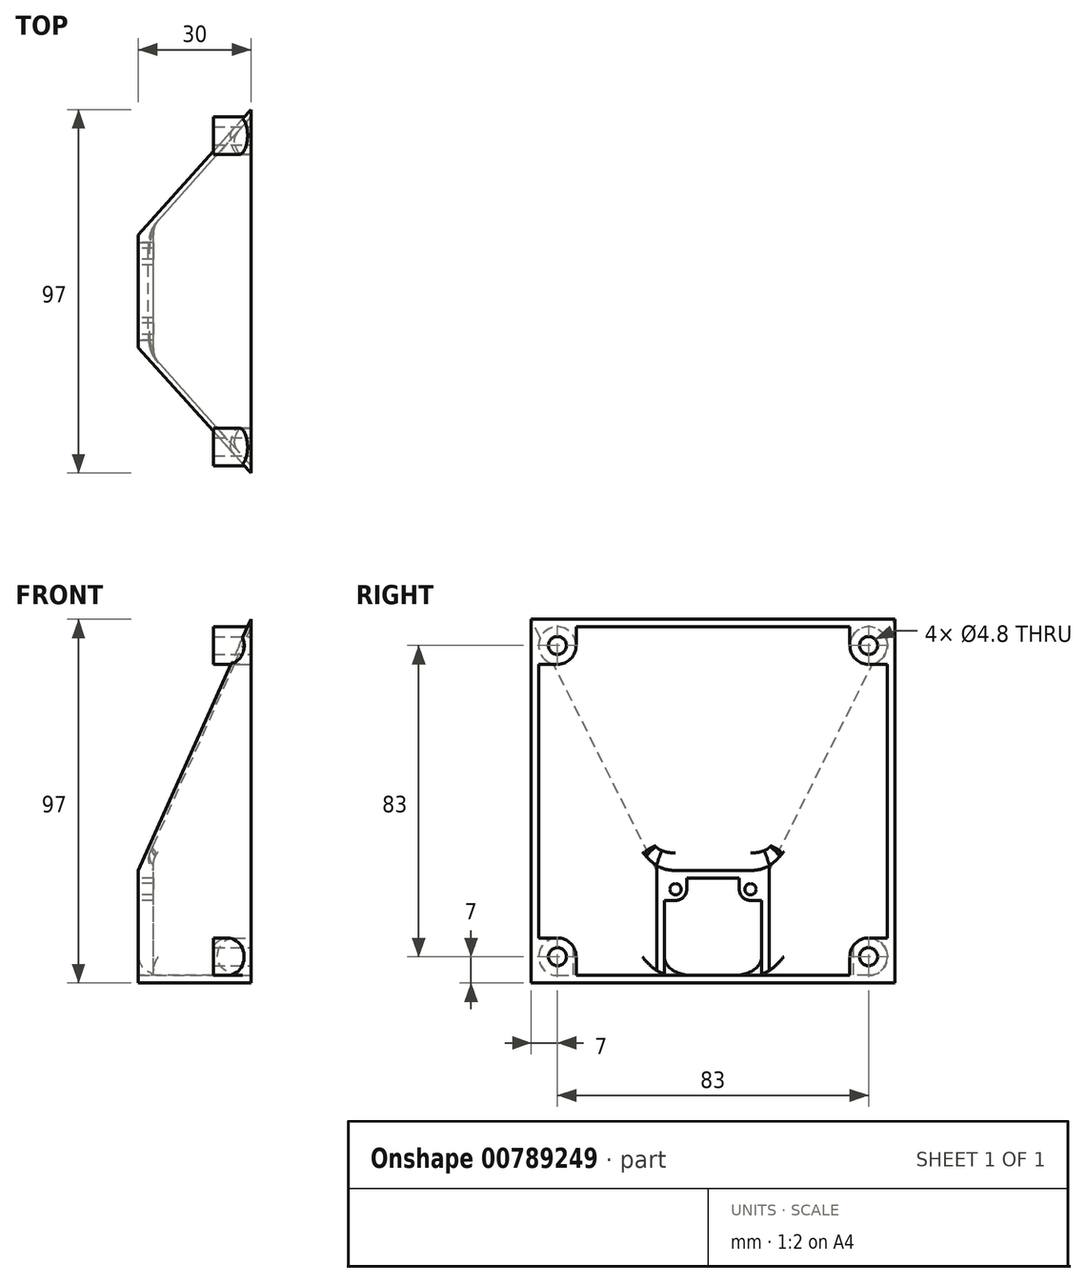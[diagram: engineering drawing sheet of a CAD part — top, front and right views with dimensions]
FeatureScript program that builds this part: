
annotation { "Feature Type Name" : "Feature", "Feature Type Description" : "" }
export const myFeature = defineFeature(function(context is Context, id is Id, definition is map)
    precondition{}
    {
        {
            var Q0;
            Q0=qCreatedBy(makeId("Right.planeOp"),FACE);
            var sketch = newSketch(context, id + "F0", { "sketchPlane" : qUnion([Q0])});
            skLineSegment(sketch, "E0.bottom", {"start": v(-15, 0) * mm, "end": v(15, 0) * mm});
            skLineSegment(sketch, "E0.top", {"start": v(-15, 30) * mm, "end": v(15, 30) * mm});
            skLineSegment(sketch, "E0.left", {"start": v(-15, 0) * mm, "end": v(-15, 30) * mm});
            skLineSegment(sketch, "E0.right", {"start": v(15, 0) * mm, "end": v(15, 30) * mm});
            skLineSegment(sketch, "E1.0", {"start": v(-13, 2) * mm, "end": v(-13, 28) * mm});
            skLineSegment(sketch, "E1.1", {"start": v(-13, 2) * mm, "end": v(13, 2) * mm});
            skLineSegment(sketch, "E1.2", {"start": v(13, 2) * mm, "end": v(13, 28) * mm});
            skLineSegment(sketch, "E1.3", {"start": v(-13, 28) * mm, "end": v(13, 28) * mm});
            skLineSegment(sketch, "E2.bottom", {"start": v(-13, 28) * mm, "end": v(-7, 28) * mm});
            skLineSegment(sketch, "E2.top", {"start": v(-13, 22) * mm, "end": v(-7, 22) * mm});
            skLineSegment(sketch, "E2.left", {"start": v(-13, 28) * mm, "end": v(-13, 22) * mm});
            skLineSegment(sketch, "E2.right", {"start": v(-7, 28) * mm, "end": v(-7, 22) * mm});
            skLineSegment(sketch, "E3.bottom", {"start": v(13, 28) * mm, "end": v(7, 28) * mm});
            skLineSegment(sketch, "E3.top", {"start": v(13, 22) * mm, "end": v(7, 22) * mm});
            skLineSegment(sketch, "E3.left", {"start": v(13, 28) * mm, "end": v(13, 22) * mm});
            skLineSegment(sketch, "E3.right", {"start": v(7, 28) * mm, "end": v(7, 22) * mm});
            skCircle(sketch, "E4", {"center": v(-10, 25) * mm, "radius": 3 * mm});
            skPoint(sketch, "E4.centerSnap0", {"position": v(-7, 25) * mm});
            skCircle(sketch, "E5", {"center": v(10, 25) * mm, "radius": 3 * mm});
            skPoint(sketch, "E5.centerSnap0", {"position": v(7, 25) * mm});
            skCircle(sketch, "E6", {"center": v(10, 25) * mm, "radius": 1.5 * mm});
            skCircle(sketch, "E7", {"center": v(-10, 25) * mm, "radius": 1.5 * mm});
            skSolve(sketch);
        }
        {
            var Q0;
            Q0=qCreatedBy(makeId("Right.planeOp"),FACE);
            cPlane(context, id + "F1", {"entities" : qUnion([Q0]), "cplaneType" : CPlaneType.OFFSET, "offset" : 30 * mm, "width" : 150 * mm, "height" : 150 * mm});
        }
        {
            var Q0;
            Q0=qCreatedBy(id+"F1.planeOp",FACE);
            var sketch = newSketch(context, id + "F2", { "sketchPlane" : qUnion([Q0])});
            skLineSegment(sketch, "E8.bottom", {"start": v(-48.5, 0) * mm, "end": v(48.5, 0) * mm});
            skLineSegment(sketch, "E8.top", {"start": v(-48.5, 97) * mm, "end": v(48.5, 97) * mm});
            skLineSegment(sketch, "E8.left", {"start": v(-48.5, 0) * mm, "end": v(-48.5, 97) * mm});
            skLineSegment(sketch, "E8.right", {"start": v(48.5, 0) * mm, "end": v(48.5, 97) * mm});
            skLineSegment(sketch, "E9.0", {"start": v(-46.5, 2) * mm, "end": v(-46.5, 95) * mm});
            skLineSegment(sketch, "E9.1", {"start": v(-46.5, 2) * mm, "end": v(46.5, 2) * mm});
            skLineSegment(sketch, "E9.2", {"start": v(46.5, 2) * mm, "end": v(46.5, 95) * mm});
            skLineSegment(sketch, "E9.3", {"start": v(-46.5, 95) * mm, "end": v(46.5, 95) * mm});
            skLineSegment(sketch, "E10.bottom", {"start": v(-46.5, 95) * mm, "end": v(-36.5, 95) * mm});
            skLineSegment(sketch, "E10.top", {"start": v(-46.5, 85) * mm, "end": v(-36.5, 85) * mm});
            skLineSegment(sketch, "E10.left", {"start": v(-46.5, 95) * mm, "end": v(-46.5, 85) * mm});
            skLineSegment(sketch, "E10.right", {"start": v(-36.5, 95) * mm, "end": v(-36.5, 85) * mm});
            skLineSegment(sketch, "E11.bottom", {"start": v(46.5, 95) * mm, "end": v(36.5, 95) * mm});
            skLineSegment(sketch, "E11.top", {"start": v(46.5, 85) * mm, "end": v(36.5, 85) * mm});
            skLineSegment(sketch, "E11.left", {"start": v(46.5, 95) * mm, "end": v(46.5, 85) * mm});
            skLineSegment(sketch, "E11.right", {"start": v(36.5, 95) * mm, "end": v(36.5, 85) * mm});
            skLineSegment(sketch, "E12.bottom", {"start": v(46.5, 2) * mm, "end": v(36.5, 2) * mm});
            skLineSegment(sketch, "E12.top", {"start": v(46.5, 12) * mm, "end": v(36.5, 12) * mm});
            skLineSegment(sketch, "E12.left", {"start": v(46.5, 2) * mm, "end": v(46.5, 12) * mm});
            skLineSegment(sketch, "E12.right", {"start": v(36.5, 2) * mm, "end": v(36.5, 12) * mm});
            skLineSegment(sketch, "E13.bottom", {"start": v(-46.5, 2) * mm, "end": v(-36.5, 2) * mm});
            skLineSegment(sketch, "E13.top", {"start": v(-46.5, 12) * mm, "end": v(-36.5, 12) * mm});
            skLineSegment(sketch, "E13.left", {"start": v(-46.5, 2) * mm, "end": v(-46.5, 12) * mm});
            skLineSegment(sketch, "E13.right", {"start": v(-36.5, 2) * mm, "end": v(-36.5, 12) * mm});
            skCircle(sketch, "E14", {"center": v(-41.5, 90) * mm, "radius": 5 * mm});
            skPoint(sketch, "E14.centerSnap0", {"position": v(-46.5, 90) * mm});
            skCircle(sketch, "E15", {"center": v(41.5, 90) * mm, "radius": 5 * mm});
            skPoint(sketch, "E15.centerSnap0", {"position": v(41.5, 85) * mm});
            skCircle(sketch, "E16", {"center": v(-41.5, 7) * mm, "radius": 5 * mm});
            skCircle(sketch, "E17", {"center": v(41.5, 7) * mm, "radius": 5 * mm});
            skPoint(sketch, "E17.centerSnap0", {"position": v(41.5, 2) * mm});
            skCircle(sketch, "E18", {"center": v(-41.5, 90) * mm, "radius": 2.4 * mm});
            skCircle(sketch, "E19", {"center": v(41.5, 90) * mm, "radius": 2.4 * mm});
            skCircle(sketch, "E20", {"center": v(41.5, 7) * mm, "radius": 2.4 * mm});
            skCircle(sketch, "E21", {"center": v(-41.5, 7) * mm, "radius": 2.4 * mm});
            skSolve(sketch);
        }
        {
            var Q0;
            Q0=qCreatedBy(makeId("Right.planeOp"),FACE);
            var sketch = newSketch(context, id + "F3", { "sketchPlane" : qUnion([Q0])});
            skLineSegment(sketch, "E22.bottom", {"start": v(-15, 0) * mm, "end": v(15, 0) * mm});
            skLineSegment(sketch, "E22.top", {"start": v(-15, 30) * mm, "end": v(15, 30) * mm});
            skLineSegment(sketch, "E22.left", {"start": v(-15, 0) * mm, "end": v(-15, 30) * mm});
            skLineSegment(sketch, "E22.right", {"start": v(15, 0) * mm, "end": v(15, 30) * mm});
            skSolve(sketch);
        }
        {
            var Q0;
            Q0=qCreatedBy(id+"F1.planeOp",FACE);
            var sketch = newSketch(context, id + "F4", { "sketchPlane" : qUnion([Q0])});
            skLineSegment(sketch, "E23.bottom", {"start": v(-48.5, 0) * mm, "end": v(48.5, 0) * mm});
            skLineSegment(sketch, "E23.top", {"start": v(-48.5, 97) * mm, "end": v(48.5, 97) * mm});
            skLineSegment(sketch, "E23.left", {"start": v(-48.5, 0) * mm, "end": v(-48.5, 97) * mm});
            skLineSegment(sketch, "E23.right", {"start": v(48.5, 0) * mm, "end": v(48.5, 97) * mm});
            skSolve(sketch);
        }
        {
            var Q0;
            Q0=qCreatedBy(makeId("Right.planeOp"),FACE);
            var sketch = newSketch(context, id + "F5", { "sketchPlane" : qUnion([Q0])});
            skLineSegment(sketch, "E24.bottom", {"start": v(-13, 2) * mm, "end": v(13, 2) * mm});
            skLineSegment(sketch, "E24.top", {"start": v(-13, 28) * mm, "end": v(13, 28) * mm});
            skLineSegment(sketch, "E24.left", {"start": v(-13, 2) * mm, "end": v(-13, 28) * mm});
            skLineSegment(sketch, "E24.right", {"start": v(13, 2) * mm, "end": v(13, 28) * mm});
            skSolve(sketch);
        }
        {
            var Q0;
            Q0=qCreatedBy(id+"F1.planeOp",FACE);
            var sketch = newSketch(context, id + "F6", { "sketchPlane" : qUnion([Q0])});
            skLineSegment(sketch, "E25.bottom", {"start": v(-46.5, 2) * mm, "end": v(46.5, 2) * mm});
            skLineSegment(sketch, "E25.top", {"start": v(-46.5, 95) * mm, "end": v(46.5, 95) * mm});
            skLineSegment(sketch, "E25.left", {"start": v(-46.5, 2) * mm, "end": v(-46.5, 95) * mm});
            skLineSegment(sketch, "E25.right", {"start": v(46.5, 2) * mm, "end": v(46.5, 95) * mm});
            skSolve(sketch);
        }
        {
            var Q0;
            Q0 = qSketchRegion(id + "F3", true);
            var Q1;
            Q1 = qSketchRegion(id + "F4", true);
            loft(context, id + "F7", {"sheetProfilesArray" : [{ "sheetProfileEntities" : qUnion([Q0]) }, { "sheetProfileEntities" : qUnion([Q1]) }]});
        }
        {
            var Q1;
            Q1 = qSketchRegion(id + "F5", true);
            var Q2;
            Q2 = qSketchRegion(id + "F6", true);
            loft(context, id + "F8", {"operationType" : NewBodyOperationType.REMOVE, "sheetProfilesArray" : [{ "sheetProfileEntities" : qUnion([Q1]) }, { "sheetProfileEntities" : qUnion([Q2]) }]});
        }
        {
            var Q0;
            Q0=makeQuery(id+"F2.imprint","IMPRINT",FACE,{"disambiguationData":[TD([[makeQuery(id+"F2.imprint","IMPRINT",EDGE,{"derivedFrom":sQuery(id+"F2.wireOp",EDGE,"E18")}),-1.0]])]});
            var Q1;
            {var subQ0=sQuery(id+"F2.wireOp",EDGE,"E10.right");var subQ1=sQuery(id+"F2.wireOp",EDGE,"E9.3");var subQ2=makeQuery(id+"F2.imprint","INTERSECT",VERTEX,{"derivedFrom":[subQ1,subQ0]});Q1=makeQuery(id+"F2.imprint","IMPRINT",FACE,{"disambiguationData":[TD([[makeQuery(id+"F2.imprint","IMPRINT",EDGE,{"disambiguationData":[TD([[subQ2,1.0]])],"derivedFrom":subQ1}),-1.0]])]});}
            var Q2;
            {var subQ0=sQuery(id+"F2.wireOp",EDGE,"E9.3");var subQ1=sQuery(id+"F2.wireOp",EDGE,"E9.0");var subQ2=makeQuery(id+"F2.imprint","INTERSECT",VERTEX,{"derivedFrom":[subQ1,subQ0]});Q2=makeQuery(id+"F2.imprint","IMPRINT",FACE,{"disambiguationData":[TD([[makeQuery(id+"F2.imprint","IMPRINT",EDGE,{"disambiguationData":[TD([[subQ2,1.0]])],"derivedFrom":subQ1}),-1.0]])]});}
            var Q3;
            {var subQ0=sQuery(id+"F2.wireOp",EDGE,"E10.top");var subQ1=sQuery(id+"F2.wireOp",EDGE,"E9.0");var subQ2=makeQuery(id+"F2.imprint","INTERSECT",VERTEX,{"derivedFrom":[subQ1,subQ0]});Q3=makeQuery(id+"F2.imprint","IMPRINT",FACE,{"disambiguationData":[TD([[makeQuery(id+"F2.imprint","IMPRINT",EDGE,{"disambiguationData":[TD([[subQ2,-1.0]])],"derivedFrom":subQ1}),-1.0]])]});}
            var Q4;
            Q4=makeQuery(id+"F2.imprint","IMPRINT",FACE,{"disambiguationData":[TD([[makeQuery(id+"F2.imprint","IMPRINT",EDGE,{"derivedFrom":sQuery(id+"F2.wireOp",EDGE,"E21")}),-1.0]])]});
            var Q5;
            {var subQ0=sQuery(id+"F2.wireOp",EDGE,"E13.top");var subQ1=sQuery(id+"F2.wireOp",EDGE,"E9.0");var subQ2=makeQuery(id+"F2.imprint","INTERSECT",VERTEX,{"derivedFrom":[subQ1,subQ0]});Q5=makeQuery(id+"F2.imprint","IMPRINT",FACE,{"disambiguationData":[TD([[makeQuery(id+"F2.imprint","IMPRINT",EDGE,{"disambiguationData":[TD([[subQ2,1.0]])],"derivedFrom":subQ1}),-1.0]])]});}
            var Q6;
            {var subQ0=sQuery(id+"F2.wireOp",EDGE,"E16");var subQ1=sQuery(id+"F2.wireOp",EDGE,"E9.0");var subQ2=makeQuery(id+"F2.imprint","INTERSECT",VERTEX,{"derivedFrom":[subQ1,subQ0]});Q6=makeQuery(id+"F2.imprint","IMPRINT",FACE,{"disambiguationData":[TD([[makeQuery(id+"F2.imprint","IMPRINT",EDGE,{"disambiguationData":[TD([[subQ2,1.0]])],"derivedFrom":subQ1}),-1.0]])]});}
            var Q7;
            {var subQ0=sQuery(id+"F2.wireOp",EDGE,"E13.right");var subQ1=sQuery(id+"F2.wireOp",EDGE,"E9.1");var subQ2=makeQuery(id+"F2.imprint","INTERSECT",VERTEX,{"derivedFrom":[subQ1,subQ0]});Q7=makeQuery(id+"F2.imprint","IMPRINT",FACE,{"disambiguationData":[TD([[makeQuery(id+"F2.imprint","IMPRINT",EDGE,{"disambiguationData":[TD([[subQ2,1.0]])],"derivedFrom":subQ1}),1.0]])]});}
            var Q8;
            Q8=makeQuery(id+"F2.imprint","IMPRINT",FACE,{"disambiguationData":[TD([[makeQuery(id+"F2.imprint","IMPRINT",EDGE,{"derivedFrom":sQuery(id+"F2.wireOp",EDGE,"E20")}),-1.0]])]});
            var Q9;
            {var subQ0=sQuery(id+"F2.wireOp",EDGE,"E12.right");var subQ1=sQuery(id+"F2.wireOp",EDGE,"E9.1");var subQ2=makeQuery(id+"F2.imprint","INTERSECT",VERTEX,{"derivedFrom":[subQ1,subQ0]});Q9=makeQuery(id+"F2.imprint","IMPRINT",FACE,{"disambiguationData":[TD([[makeQuery(id+"F2.imprint","IMPRINT",EDGE,{"disambiguationData":[TD([[subQ2,-1.0]])],"derivedFrom":subQ1}),1.0]])]});}
            var Q10;
            {var subQ0=sQuery(id+"F2.wireOp",EDGE,"E9.2");var subQ1=sQuery(id+"F2.wireOp",EDGE,"E9.1");var subQ2=makeQuery(id+"F2.imprint","INTERSECT",VERTEX,{"derivedFrom":[subQ1,subQ0]});Q10=makeQuery(id+"F2.imprint","IMPRINT",FACE,{"disambiguationData":[TD([[makeQuery(id+"F2.imprint","IMPRINT",EDGE,{"disambiguationData":[TD([[subQ2,1.0]])],"derivedFrom":subQ1}),1.0]])]});}
            var Q11;
            {var subQ0=sQuery(id+"F2.wireOp",EDGE,"E12.top");var subQ1=sQuery(id+"F2.wireOp",EDGE,"E9.2");var subQ2=makeQuery(id+"F2.imprint","INTERSECT",VERTEX,{"derivedFrom":[subQ1,subQ0]});Q11=makeQuery(id+"F2.imprint","IMPRINT",FACE,{"disambiguationData":[TD([[makeQuery(id+"F2.imprint","IMPRINT",EDGE,{"disambiguationData":[TD([[subQ2,1.0]])],"derivedFrom":subQ1}),1.0]])]});}
            var Q12;
            Q12=makeQuery(id+"F2.imprint","IMPRINT",FACE,{"disambiguationData":[TD([[makeQuery(id+"F2.imprint","IMPRINT",EDGE,{"derivedFrom":sQuery(id+"F2.wireOp",EDGE,"E19")}),-1.0]])]});
            var Q13;
            {var subQ0=sQuery(id+"F2.wireOp",EDGE,"E11.right");var subQ1=sQuery(id+"F2.wireOp",EDGE,"E9.3");var subQ2=makeQuery(id+"F2.imprint","INTERSECT",VERTEX,{"derivedFrom":[subQ1,subQ0]});Q13=makeQuery(id+"F2.imprint","IMPRINT",FACE,{"disambiguationData":[TD([[makeQuery(id+"F2.imprint","IMPRINT",EDGE,{"disambiguationData":[TD([[subQ2,-1.0]])],"derivedFrom":subQ1}),-1.0]])]});}
            var Q14;
            {var subQ0=sQuery(id+"F2.wireOp",EDGE,"E9.3");var subQ1=sQuery(id+"F2.wireOp",EDGE,"E9.2");var subQ2=makeQuery(id+"F2.imprint","INTERSECT",VERTEX,{"derivedFrom":[subQ1,subQ0]});Q14=makeQuery(id+"F2.imprint","IMPRINT",FACE,{"disambiguationData":[TD([[makeQuery(id+"F2.imprint","IMPRINT",EDGE,{"disambiguationData":[TD([[subQ2,1.0]])],"derivedFrom":subQ1}),1.0]])]});}
            var Q15;
            {var subQ0=sQuery(id+"F2.wireOp",EDGE,"E11.top");var subQ1=sQuery(id+"F2.wireOp",EDGE,"E9.2");var subQ2=makeQuery(id+"F2.imprint","INTERSECT",VERTEX,{"derivedFrom":[subQ1,subQ0]});Q15=makeQuery(id+"F2.imprint","IMPRINT",FACE,{"disambiguationData":[TD([[makeQuery(id+"F2.imprint","IMPRINT",EDGE,{"disambiguationData":[TD([[subQ2,-1.0]])],"derivedFrom":subQ1}),1.0]])]});}
            extrude(context, id + "F9", {"entities" : qUnion([Q0, Q1, Q2, Q3, Q4, Q5, Q6, Q7, Q8, Q9, Q10, Q11, Q12, Q13, Q14, Q15]), "operationType" : NewBodyOperationType.ADD, "oppositeDirection" : true, "depth" : 10 * mm, "offsetDistance" : 25 * mm});
        }
        {
            var Q0;
            Q0=makeQuery(id+"F0.imprint","IMPRINT",FACE,{"disambiguationData":[TD([[makeQuery(id+"F0.imprint","IMPRINT",EDGE,{"derivedFrom":sQuery(id+"F0.wireOp",EDGE,"E7")}),-1.0]])]});
            var Q1;
            {var subQ0=sQuery(id+"F0.wireOp",EDGE,"E2.right");var subQ1=sQuery(id+"F0.wireOp",EDGE,"E1.3");var subQ2=makeQuery(id+"F0.imprint","INTERSECT",VERTEX,{"derivedFrom":[subQ1,subQ0]});Q1=makeQuery(id+"F0.imprint","IMPRINT",FACE,{"disambiguationData":[TD([[makeQuery(id+"F0.imprint","IMPRINT",EDGE,{"disambiguationData":[TD([[subQ2,1.0]])],"derivedFrom":subQ1}),-1.0]])]});}
            var Q2;
            {var subQ0=sQuery(id+"F0.wireOp",EDGE,"E4");var subQ1=sQuery(id+"F0.wireOp",EDGE,"E1.0");var subQ2=makeQuery(id+"F0.imprint","INTERSECT",VERTEX,{"derivedFrom":[subQ1,subQ0]});Q2=makeQuery(id+"F0.imprint","IMPRINT",FACE,{"disambiguationData":[TD([[makeQuery(id+"F0.imprint","IMPRINT",EDGE,{"disambiguationData":[TD([[subQ2,-1.0]])],"derivedFrom":subQ1}),-1.0]])]});}
            var Q3;
            {var subQ0=sQuery(id+"F0.wireOp",EDGE,"E4");var subQ1=sQuery(id+"F0.wireOp",EDGE,"E1.0");var subQ2=makeQuery(id+"F0.imprint","INTERSECT",VERTEX,{"derivedFrom":[subQ1,subQ0]});Q3=makeQuery(id+"F0.imprint","IMPRINT",FACE,{"disambiguationData":[TD([[makeQuery(id+"F0.imprint","IMPRINT",EDGE,{"disambiguationData":[TD([[subQ2,1.0]])],"derivedFrom":subQ1}),-1.0]])]});}
            var Q4;
            {var subQ0=sQuery(id+"F0.wireOp",EDGE,"E5");var subQ1=sQuery(id+"F0.wireOp",EDGE,"E1.3");var subQ2=makeQuery(id+"F0.imprint","INTERSECT",VERTEX,{"derivedFrom":[subQ1,subQ0]});Q4=makeQuery(id+"F0.imprint","IMPRINT",FACE,{"disambiguationData":[TD([[makeQuery(id+"F0.imprint","IMPRINT",EDGE,{"disambiguationData":[TD([[subQ2,1.0]])],"derivedFrom":subQ1}),-1.0]])]});}
            var Q5;
            {var subQ0=sQuery(id+"F0.wireOp",EDGE,"E5");var subQ1=sQuery(id+"F0.wireOp",EDGE,"E1.2");var subQ2=makeQuery(id+"F0.imprint","INTERSECT",VERTEX,{"derivedFrom":[subQ1,subQ0]});Q5=makeQuery(id+"F0.imprint","IMPRINT",FACE,{"disambiguationData":[TD([[makeQuery(id+"F0.imprint","IMPRINT",EDGE,{"disambiguationData":[TD([[subQ2,-1.0]])],"derivedFrom":subQ1}),1.0]])]});}
            var Q6;
            {var subQ0=sQuery(id+"F0.wireOp",EDGE,"E5");var subQ1=sQuery(id+"F0.wireOp",EDGE,"E1.2");var subQ2=makeQuery(id+"F0.imprint","INTERSECT",VERTEX,{"derivedFrom":[subQ1,subQ0]});Q6=makeQuery(id+"F0.imprint","IMPRINT",FACE,{"disambiguationData":[TD([[makeQuery(id+"F0.imprint","IMPRINT",EDGE,{"disambiguationData":[TD([[subQ2,1.0]])],"derivedFrom":subQ1}),1.0]])]});}
            var Q7;
            Q7=makeQuery(id+"F0.imprint","IMPRINT",FACE,{"disambiguationData":[TD([[makeQuery(id+"F0.imprint","IMPRINT",EDGE,{"derivedFrom":sQuery(id+"F0.wireOp",EDGE,"E6")}),-1.0]])]});
            var Q8;
            Q8=makeQuery(id+"F0.imprint","IMPRINT",FACE,{"disambiguationData":[TD([[makeQuery(id+"F0.imprint","IMPRINT",EDGE,{"derivedFrom":sQuery(id+"F0.wireOp",EDGE,"E0.bottom")}),1.0]])]});
            extrude(context, id + "F10", {"entities" : qUnion([Q0, Q1, Q2, Q3, Q4, Q5, Q6, Q7, Q8]), "operationType" : NewBodyOperationType.ADD, "depth" : 4 * mm, "offsetDistance" : 25 * mm});
        }
        {
            var Q0;
            {var subQ6=sQuery(id+"F2.wireOp",EDGE,"E11.top");var subQ9=sQuery(id+"F6.wireOp",EDGE,"E25.right");var subQ11=sQuery(id+"F6.wireOp",EDGE,"E25.top");var subQ12=sQuery(id+"F5.wireOp",EDGE,"E24.right");var subQ14=sQuery(id+"F5.wireOp",EDGE,"E24.top");var subQ15=sQuery(id+"F6.wireOp",EDGE,"E25.bottom");var subQ16=sQuery(id+"F5.wireOp",EDGE,"E24.bottom");Q0=makeQuery(id+"F10.boolean.opBoolean","INTERSECT",EDGE,{"derivedFrom":[makeQuery(id+"F9.boolean.opBoolean","SPLIT",FACE,{"disambiguationData":[TD([makeQuery(id+"F9.opExtrude","SWEPT_FACE",FACE,{"disambiguationData":[OSD([subQ6])]})])],"derivedFrom":makeQuery(id+"F8.boolean.opBoolean","COPY",FACE,{"derivedFrom":makeQuery(id+"F8.opLoft","SWEPT_FACE",FACE,{"disambiguationData":[OSD([subQ16,subQ14,subQ12,subQ15,subQ11,subQ9])]})})}),makeQuery(id+"F10.opExtrude","SWEPT_FACE",FACE,{"disambiguationData":[OSD([sQuery(id+"F0.wireOp",EDGE,"E0.right")])]})]});}
            var Q1;
            {var subQ6=sQuery(id+"F2.wireOp",EDGE,"E11.top");var subQ9=sQuery(id+"F6.wireOp",EDGE,"E25.right");var subQ11=sQuery(id+"F6.wireOp",EDGE,"E25.top");var subQ12=sQuery(id+"F5.wireOp",EDGE,"E24.right");var subQ14=sQuery(id+"F5.wireOp",EDGE,"E24.top");var subQ15=sQuery(id+"F6.wireOp",EDGE,"E25.bottom");var subQ16=sQuery(id+"F5.wireOp",EDGE,"E24.bottom");Q1=makeQuery(id+"F10.boolean.opBoolean","INTERSECT",EDGE,{"derivedFrom":[makeQuery(id+"F9.boolean.opBoolean","SPLIT",FACE,{"disambiguationData":[TD([makeQuery(id+"F9.opExtrude","SWEPT_FACE",FACE,{"disambiguationData":[OSD([subQ6])]})])],"derivedFrom":makeQuery(id+"F8.boolean.opBoolean","COPY",FACE,{"derivedFrom":makeQuery(id+"F8.opLoft","SWEPT_FACE",FACE,{"disambiguationData":[OSD([subQ16,subQ14,subQ12,subQ15,subQ11,subQ9])]})})}),makeQuery(id+"F10.opExtrude","SWEPT_FACE",FACE,{"disambiguationData":[OSD([sQuery(id+"F0.wireOp",EDGE,"E0.top")])]})]});}
            var Q2;
            {var subQ1=sQuery(id+"F2.wireOp",EDGE,"E10.top");var subQ10=sQuery(id+"F6.wireOp",EDGE,"E25.left");var subQ11=sQuery(id+"F6.wireOp",EDGE,"E25.top");var subQ13=sQuery(id+"F5.wireOp",EDGE,"E24.left");var subQ14=sQuery(id+"F5.wireOp",EDGE,"E24.top");var subQ15=sQuery(id+"F6.wireOp",EDGE,"E25.bottom");var subQ16=sQuery(id+"F5.wireOp",EDGE,"E24.bottom");Q2=makeQuery(id+"F10.boolean.opBoolean","INTERSECT",EDGE,{"derivedFrom":[makeQuery(id+"F9.boolean.opBoolean","SPLIT",FACE,{"disambiguationData":[TD([makeQuery(id+"F9.opExtrude","SWEPT_FACE",FACE,{"disambiguationData":[OSD([subQ1])]})])],"derivedFrom":makeQuery(id+"F8.boolean.opBoolean","COPY",FACE,{"derivedFrom":makeQuery(id+"F8.opLoft","SWEPT_FACE",FACE,{"disambiguationData":[OSD([subQ16,subQ14,subQ13,subQ15,subQ11,subQ10])]})})}),makeQuery(id+"F10.opExtrude","SWEPT_FACE",FACE,{"disambiguationData":[OSD([sQuery(id+"F0.wireOp",EDGE,"E0.left")])]})]});}
            var Q3;
            {var subQ1=sQuery(id+"F2.wireOp",EDGE,"E10.top");var subQ10=sQuery(id+"F6.wireOp",EDGE,"E25.left");var subQ11=sQuery(id+"F6.wireOp",EDGE,"E25.top");var subQ13=sQuery(id+"F5.wireOp",EDGE,"E24.left");var subQ14=sQuery(id+"F5.wireOp",EDGE,"E24.top");var subQ15=sQuery(id+"F6.wireOp",EDGE,"E25.bottom");var subQ16=sQuery(id+"F5.wireOp",EDGE,"E24.bottom");Q3=makeQuery(id+"F10.boolean.opBoolean","INTERSECT",EDGE,{"derivedFrom":[makeQuery(id+"F9.boolean.opBoolean","SPLIT",FACE,{"disambiguationData":[TD([makeQuery(id+"F9.opExtrude","SWEPT_FACE",FACE,{"disambiguationData":[OSD([subQ1])]})])],"derivedFrom":makeQuery(id+"F8.boolean.opBoolean","COPY",FACE,{"derivedFrom":makeQuery(id+"F8.opLoft","SWEPT_FACE",FACE,{"disambiguationData":[OSD([subQ16,subQ14,subQ13,subQ15,subQ11,subQ10])]})})}),makeQuery(id+"F10.opExtrude","SWEPT_FACE",FACE,{"disambiguationData":[OSD([sQuery(id+"F0.wireOp",EDGE,"E0.top")])]})]});}
            fillet(context, id + "F11", {"entities" : qUnion([Q0, Q1, Q2, Q3]), "radius" : 5 * mm, "tangentPropagation" : true, "allowEdgeOverflow" : false});
        }
        {
            var Q0;
            {var subQ1=sQuery(id+"F2.wireOp",EDGE,"E10.top");var subQ2=sQuery(id+"F6.wireOp",EDGE,"E25.right");var subQ3=sQuery(id+"F6.wireOp",EDGE,"E25.top");var subQ5=sQuery(id+"F5.wireOp",EDGE,"E24.right");var subQ6=sQuery(id+"F5.wireOp",EDGE,"E24.top");var subQ16=sQuery(id+"F6.wireOp",EDGE,"E25.left");var subQ17=sQuery(id+"F5.wireOp",EDGE,"E24.left");Q0=makeQuery(id+"F10.boolean.opBoolean","INTERSECT",EDGE,{"derivedFrom":[makeQuery(id+"F9.boolean.opBoolean","SPLIT",FACE,{"disambiguationData":[TD([makeQuery(id+"F9.opExtrude","SWEPT_FACE",FACE,{"disambiguationData":[OSD([subQ1])]})])],"derivedFrom":makeQuery(id+"F8.boolean.opBoolean","COPY",FACE,{"derivedFrom":makeQuery(id+"F8.opLoft","SWEPT_FACE",FACE,{"disambiguationData":[OSD([subQ6,subQ17,subQ5,subQ3,subQ16,subQ2])]})})}),makeQuery(id+"F10.opExtrude","SWEPT_FACE",FACE,{"disambiguationData":[OSD([sQuery(id+"F0.wireOp",EDGE,"E0.top")])]})]});}
            fillet(context, id + "F12", {"entities" : qUnion([Q0]), "radius" : 4 * mm, "tangentPropagation" : true, "allowEdgeOverflow" : false});
        }
        {
            var Q0;
            Q0=makeQuery(id+"F2.imprint","IMPRINT",FACE,{"disambiguationData":[TD([[makeQuery(id+"F2.imprint","IMPRINT",EDGE,{"derivedFrom":sQuery(id+"F2.wireOp",EDGE,"E18")}),1.0]])]});
            var Q1;
            Q1=makeQuery(id+"F2.imprint","IMPRINT",FACE,{"disambiguationData":[TD([[makeQuery(id+"F2.imprint","IMPRINT",EDGE,{"derivedFrom":sQuery(id+"F2.wireOp",EDGE,"E19")}),1.0]])]});
            var Q2;
            Q2=makeQuery(id+"F2.imprint","IMPRINT",FACE,{"disambiguationData":[TD([[makeQuery(id+"F2.imprint","IMPRINT",EDGE,{"derivedFrom":sQuery(id+"F2.wireOp",EDGE,"E20")}),1.0]])]});
            var Q3;
            Q3=makeQuery(id+"F2.imprint","IMPRINT",FACE,{"disambiguationData":[TD([[makeQuery(id+"F2.imprint","IMPRINT",EDGE,{"derivedFrom":sQuery(id+"F2.wireOp",EDGE,"E21")}),1.0]])]});
            extrude(context, id + "F13", {"entities" : qUnion([Q0, Q1, Q2, Q3]), "operationType" : NewBodyOperationType.REMOVE, "oppositeDirection" : true, "depth" : 25 * mm, "offsetDistance" : 25 * mm});
        }
        {
            var Q0;
            Q0=makeQuery(id+"F9.opExtrude","SWEPT_EDGE",EDGE,{"disambiguationData":[OSD([sQuery(id+"F2.wireOp",EDGE,"E9.0"),sQuery(id+"F2.wireOp",EDGE,"E13.top")])]});
            var Q1;
            Q1=makeQuery(id+"F9.opExtrude","SWEPT_EDGE",EDGE,{"disambiguationData":[OSD([sQuery(id+"F2.wireOp",EDGE,"E9.0"),sQuery(id+"F2.wireOp",EDGE,"E9.1")])]});
            var Q2;
            Q2=makeQuery(id+"F9.opExtrude","SWEPT_EDGE",EDGE,{"disambiguationData":[OSD([sQuery(id+"F2.wireOp",EDGE,"E9.0"),sQuery(id+"F2.wireOp",EDGE,"E9.3")])]});
            var Q3;
            Q3=makeQuery(id+"F9.opExtrude","SWEPT_EDGE",EDGE,{"disambiguationData":[OSD([sQuery(id+"F2.wireOp",EDGE,"E9.3"),sQuery(id+"F2.wireOp",EDGE,"E10.right")])]});
            var Q4;
            Q4=makeQuery(id+"F9.opExtrude","SWEPT_EDGE",EDGE,{"disambiguationData":[OSD([sQuery(id+"F2.wireOp",EDGE,"E9.0"),sQuery(id+"F2.wireOp",EDGE,"E10.top")])]});
            var Q5;
            Q5=makeQuery(id+"F9.opExtrude","SWEPT_EDGE",EDGE,{"disambiguationData":[OSD([sQuery(id+"F2.wireOp",EDGE,"E9.2"),sQuery(id+"F2.wireOp",EDGE,"E9.3")])]});
            var Q6;
            Q6=makeQuery(id+"F9.opExtrude","SWEPT_EDGE",EDGE,{"disambiguationData":[OSD([sQuery(id+"F2.wireOp",EDGE,"E9.2"),sQuery(id+"F2.wireOp",EDGE,"E11.top")])]});
            var Q7;
            Q7=makeQuery(id+"F9.opExtrude","SWEPT_EDGE",EDGE,{"disambiguationData":[OSD([sQuery(id+"F2.wireOp",EDGE,"E9.3"),sQuery(id+"F2.wireOp",EDGE,"E11.right")])]});
            var Q8;
            Q8=makeQuery(id+"F9.opExtrude","SWEPT_EDGE",EDGE,{"disambiguationData":[OSD([sQuery(id+"F2.wireOp",EDGE,"E9.2"),sQuery(id+"F2.wireOp",EDGE,"E12.top")])]});
            var Q9;
            Q9=makeQuery(id+"F9.opExtrude","SWEPT_EDGE",EDGE,{"disambiguationData":[OSD([sQuery(id+"F2.wireOp",EDGE,"E9.1"),sQuery(id+"F2.wireOp",EDGE,"E9.2")])]});
            fillet(context, id + "F14", {"entities" : qUnion([Q0, Q1, Q2, Q3, Q4, Q5, Q6, Q7, Q8, Q9]), "radius" : 5 * mm, "tangentPropagation" : true, "allowEdgeOverflow" : false});
        }
        {
            var Q0;
            Q0=makeQuery(id+"F8.boolean.opBoolean","COPY",EDGE,{"derivedFrom":makeQuery(id+"F8.opLoft","SWEPT_EDGE",EDGE,{"disambiguationData":[OSD([sQuery(id+"F5.wireOp",EDGE,"E24.bottom"),sQuery(id+"F5.wireOp",EDGE,"E24.left"),sQuery(id+"F6.wireOp",EDGE,"E25.bottom"),sQuery(id+"F6.wireOp",EDGE,"E25.left")])]})});
            var Q1;
            Q1=makeQuery(id+"F8.boolean.opBoolean","COPY",EDGE,{"derivedFrom":makeQuery(id+"F8.opLoft","SWEPT_EDGE",EDGE,{"disambiguationData":[OSD([sQuery(id+"F5.wireOp",EDGE,"E24.bottom"),sQuery(id+"F5.wireOp",EDGE,"E24.right"),sQuery(id+"F6.wireOp",EDGE,"E25.bottom"),sQuery(id+"F6.wireOp",EDGE,"E25.right")])]})});
            fillet(context, id + "F15", {"entities" : qUnion([Q0, Q1]), "radius" : 5 * mm, "tangentPropagation" : true, "allowEdgeOverflow" : false});
        }
    });
